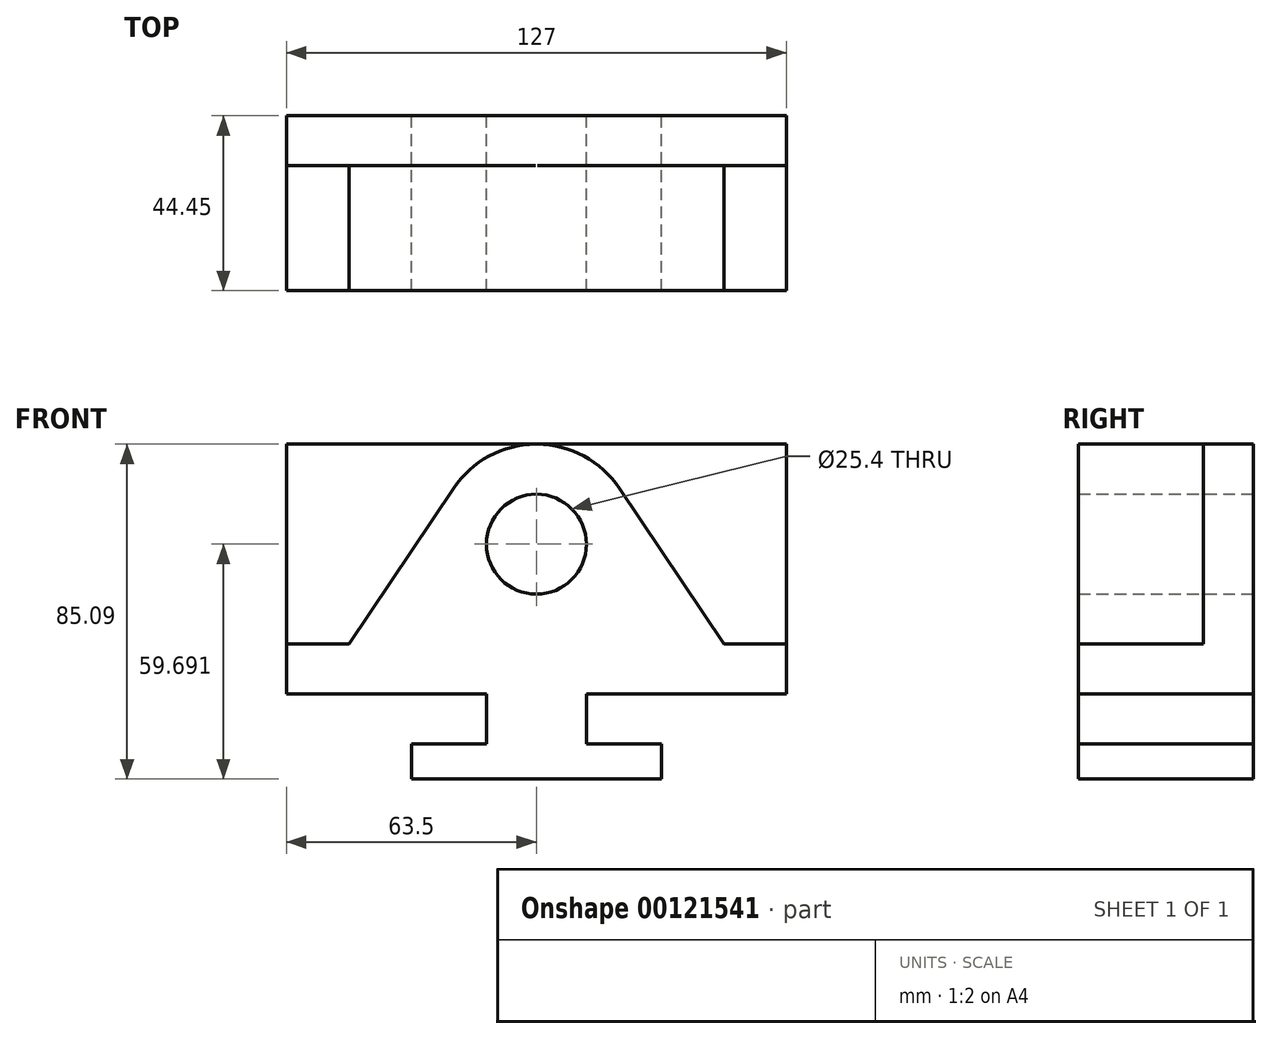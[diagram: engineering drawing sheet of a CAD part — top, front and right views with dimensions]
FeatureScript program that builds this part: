
annotation { "Feature Type Name" : "Feature", "Feature Type Description" : "" }
export const myFeature = defineFeature(function(context is Context, id is Id, definition is map)
    precondition{}
    {
        {
            var Q0;
            Q0=qCreatedBy(makeId("Front.planeOp"),FACE);
            var sketch = newSketch(context, id + "F0", { "sketchPlane" : qUnion([Q0])});
            skLineSegment(sketch, "E0", {"start": v(0, 0) * mm, "end": v(31.75, 0) * mm});
            skLineSegment(sketch, "E1", {"start": v(31.75, 0) * mm, "end": v(31.75, 8.89) * mm});
            skLineSegment(sketch, "E2", {"start": v(31.75, 8.9) * mm, "end": v(12.7, 8.9) * mm});
            skLineSegment(sketch, "E3", {"start": v(12.7, 8.89) * mm, "end": v(12.7, 21.59) * mm});
            skLineSegment(sketch, "E4", {"start": v(12.7, 21.59) * mm, "end": v(63.5, 21.6) * mm});
            skLineSegment(sketch, "E5", {"start": v(63.5, 21.59) * mm, "end": v(63.5, 34.29) * mm});
            skLineSegment(sketch, "E6", {"start": v(63.5, 34.3) * mm, "end": v(47.62, 34.3) * mm});
            skLineSegment(sketch, "E7", {"start": v(47.62, 34.29) * mm, "end": v(21.1, 73.84) * mm});
            skLineSegment(sketch, "E8", {"start": v(63.5, 34.29) * mm, "end": v(63.5, 85.1) * mm});
            skLineSegment(sketch, "E9", {"start": v(0, 0) * mm, "end": v(0, 91.05) * mm, "construction": true});
            skLineSegment(sketch, "E10", {"start": v(0, 0) * mm, "end": v(-31.75, 0) * mm});
            skLineSegment(sketch, "E11", {"start": v(-31.75, 0) * mm, "end": v(-31.75, 8.89) * mm});
            skLineSegment(sketch, "E12", {"start": v(-31.75, 8.9) * mm, "end": v(-12.7, 8.9) * mm});
            skLineSegment(sketch, "E13", {"start": v(-12.7, 8.89) * mm, "end": v(-12.7, 21.59) * mm});
            skLineSegment(sketch, "E14", {"start": v(-12.7, 21.59) * mm, "end": v(-63.5, 21.59) * mm});
            skLineSegment(sketch, "E15", {"start": v(-63.5, 21.59) * mm, "end": v(-63.5, 34.29) * mm});
            skLineSegment(sketch, "E16", {"start": v(-63.5, 34.29) * mm, "end": v(-47.62, 34.29) * mm});
            skArc(sketch, "E17", {"start": v(21.1, 73.84) * mm, "mid": v(0, 85.1) * mm, "end": v(-21.1, 73.84) * mm});
            skLineSegment(sketch, "E18", {"start": v(-47.62, 34.29) * mm, "end": v(-21.1, 73.84) * mm});
            skLineSegment(sketch, "E19", {"start": v(-63.5, 34.29) * mm, "end": v(-63.5, 85.1) * mm});
            skLineSegment(sketch, "E20", {"start": v(-63.5, 85.1) * mm, "end": v(63.5, 85.1) * mm});
            skCircle(sketch, "E21", {"center": v(0, 59.7) * mm, "radius": 12.7 * mm});
            skSolve(sketch);
        }
        {
            var Q0;
            Q0=makeQuery(id+"F0.imprint","IMPRINT",FACE,{"disambiguationData":[TD([[makeQuery(id+"F0.imprint","IMPRINT",EDGE,{"derivedFrom":sQuery(id+"F0.wireOp",EDGE,"E0")}),1.0]])]});
            extrude(context, id + "F1", {"entities" : qUnion([Q0]), "depth" : 44.45 * mm});
        }
        {
            var Q0;
            Q0 = qSketchRegion(id + "F0", true);
            extrude(context, id + "F2", {"entities" : qUnion([Q0]), "operationType" : NewBodyOperationType.ADD, "depth" : 12.7 * mm});
        }
    });
